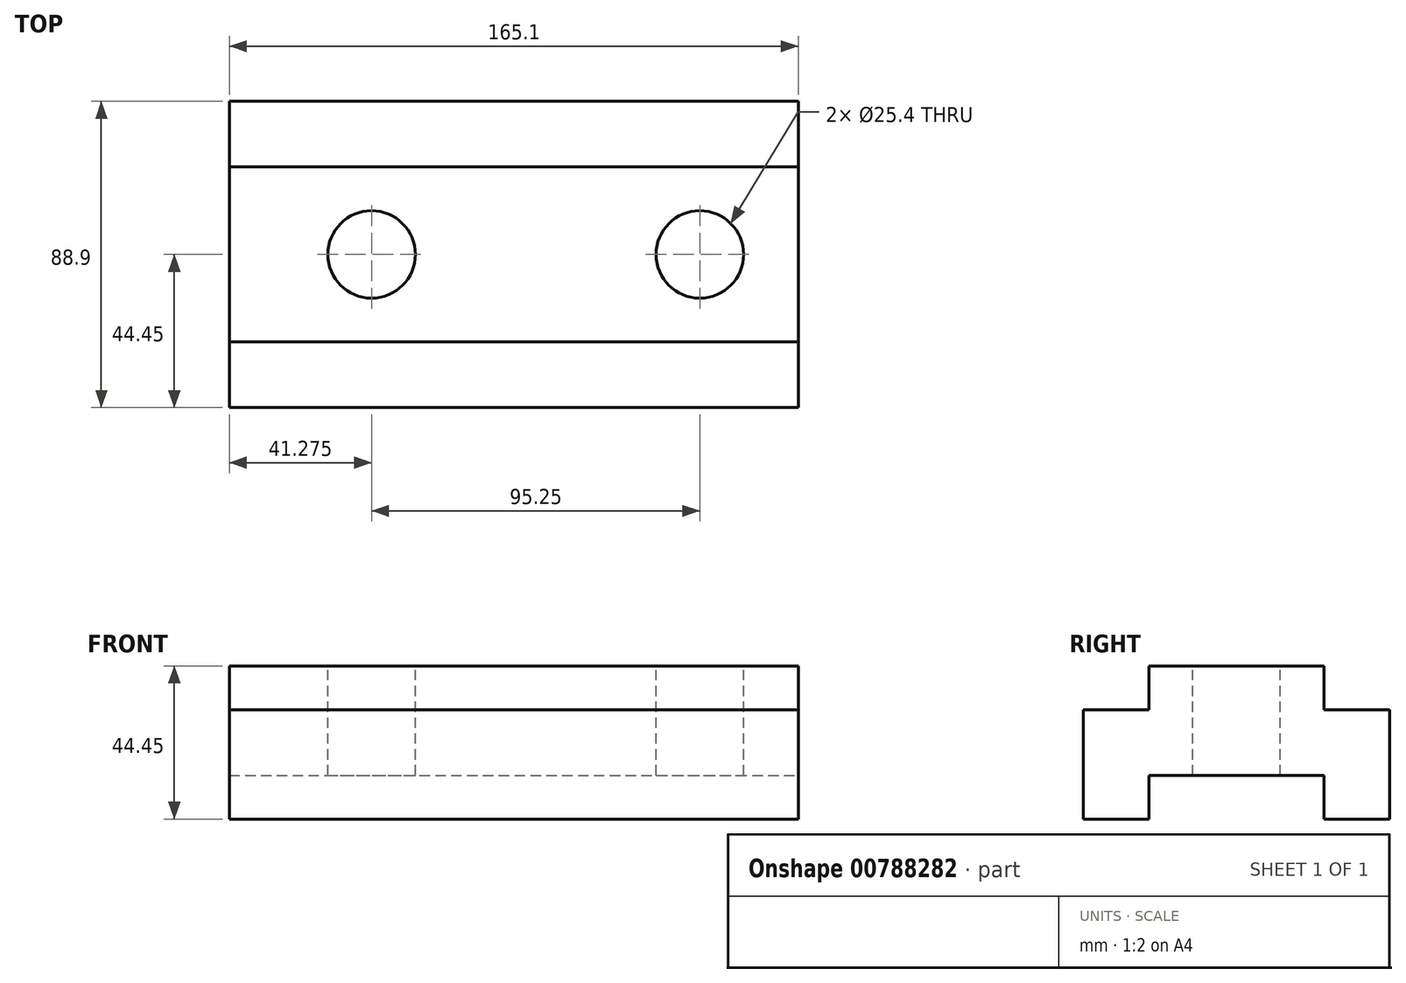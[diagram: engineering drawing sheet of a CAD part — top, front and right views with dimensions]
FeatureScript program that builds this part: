
annotation { "Feature Type Name" : "Feature", "Feature Type Description" : "" }
export const myFeature = defineFeature(function(context is Context, id is Id, definition is map)
    precondition{}
    {
        {
            var Q0;
            Q0=qCreatedBy(makeId("Right.planeOp"),FACE);
            var sketch = newSketch(context, id + "F0", { "sketchPlane" : qUnion([Q0])});
            skLineSegment(sketch, "E0", {"start": v(0, 0) * mm, "end": v(0, 31.75) * mm});
            skLineSegment(sketch, "E1", {"start": v(0, 31.75) * mm, "end": v(-19.05, 31.75) * mm});
            skLineSegment(sketch, "E2", {"start": v(-19.05, 31.75) * mm, "end": v(-19.05, 44.45) * mm});
            skLineSegment(sketch, "E3", {"start": v(-19.05, 44.45) * mm, "end": v(-69.85, 44.45) * mm});
            skLineSegment(sketch, "E4", {"start": v(-69.85, 44.45) * mm, "end": v(-69.85, 31.75) * mm});
            skLineSegment(sketch, "E5", {"start": v(-69.85, 31.75) * mm, "end": v(-88.9, 31.75) * mm});
            skLineSegment(sketch, "E6", {"start": v(-88.9, 31.75) * mm, "end": v(-88.9, 0) * mm});
            skLineSegment(sketch, "E7", {"start": v(-88.9, 0) * mm, "end": v(0, 0) * mm});
            skSolve(sketch);
        }
        {
            var Q0;
            Q0=makeQuery(id+"F0.imprint","IMPRINT",FACE,{"disambiguationData":[TD([[makeQuery(id+"F0.imprint","IMPRINT",EDGE,{"derivedFrom":sQuery(id+"F0.wireOp",EDGE,"E0")}),1.0]])]});
            extrude(context, id + "F1", {"entities" : qUnion([Q0]), "depth" : 165.1 * mm, "offsetDistance" : 25.4 * mm});
        }
        {
            var Q0;
            Q0=makeQuery(id+"F1.opExtrude","CAP_FACE",FACE,{"disambiguationData":[OSD([sQuery(id+"F0.wireOp",EDGE,"E0"),sQuery(id+"F0.wireOp",EDGE,"E1"),sQuery(id+"F0.wireOp",EDGE,"E2"),sQuery(id+"F0.wireOp",EDGE,"E3"),sQuery(id+"F0.wireOp",EDGE,"E4"),sQuery(id+"F0.wireOp",EDGE,"E5"),sQuery(id+"F0.wireOp",EDGE,"E6"),sQuery(id+"F0.wireOp",EDGE,"E7")])],"isStart":false});
            var sketch = newSketch(context, id + "F2", { "sketchPlane" : qUnion([Q0])});
            skLineSegment(sketch, "E8", {"start": v(-88.9, 0) * mm, "end": v(-69.85, 0) * mm});
            skLineSegment(sketch, "E9", {"start": v(-69.85, 0) * mm, "end": v(-69.85, 12.7) * mm});
            skLineSegment(sketch, "E10", {"start": v(-69.85, 12.7) * mm, "end": v(-19.05, 12.7) * mm});
            skLineSegment(sketch, "E11", {"start": v(-19.05, 12.7) * mm, "end": v(-19.05, 0) * mm});
            skLineSegment(sketch, "E12", {"start": v(-19.05, 0) * mm, "end": v(0, 0) * mm});
            skSolve(sketch);
        }
        {
            var Q0;
            {var subQ0=sQuery(id+"F2.wireOp",EDGE,"E9");Q0=makeQuery(id+"F2.imprint","IMPRINT",FACE,{"disambiguationData":[TD([[makeQuery(id+"F2.imprint","IMPRINT",EDGE,{"derivedFrom":subQ0}),-1.0]])]});}
            extrude(context, id + "F3", {"entities" : qUnion([Q0]), "operationType" : NewBodyOperationType.REMOVE, "oppositeDirection" : true, "depth" : 165.1 * mm, "offsetDistance" : 25.4 * mm});
        }
        {
            var Q0;
            Q0=makeQuery(id+"F1.opExtrude","SWEPT_FACE",FACE,{"disambiguationData":[OSD([sQuery(id+"F0.wireOp",EDGE,"E3")])]});
            var sketch = newSketch(context, id + "F4", { "sketchPlane" : qUnion([Q0])});
            skLineSegment(sketch, "E13", {"start": v(0, -19.05) * mm, "end": v(0, -44.45) * mm, "construction": true});
            skLineSegment(sketch, "E14", {"start": v(0, -44.45) * mm, "end": v(41.28, -44.45) * mm, "construction": true});
            skLineSegment(sketch, "E15", {"start": v(41.28, -44.45) * mm, "end": v(136.53, -44.45) * mm, "construction": true});
            skCircle(sketch, "E16", {"center": v(41.28, -44.45) * mm, "radius": 12.7 * mm});
            skCircle(sketch, "E17", {"center": v(136.53, -44.45) * mm, "radius": 12.7 * mm});
            skSolve(sketch);
        }
        {
            var Q0;
            Q0=makeQuery(id+"F4.imprint","IMPRINT",FACE,{"disambiguationData":[TD([[makeQuery(id+"F4.imprint","IMPRINT",EDGE,{"derivedFrom":sQuery(id+"F4.wireOp",EDGE,"E16")}),1.0]])]});
            var Q1;
            Q1=makeQuery(id+"F4.imprint","IMPRINT",FACE,{"disambiguationData":[TD([[makeQuery(id+"F4.imprint","IMPRINT",EDGE,{"derivedFrom":sQuery(id+"F4.wireOp",EDGE,"E17")}),1.0]])]});
            extrude(context, id + "F5", {"entities" : qUnion([Q0, Q1]), "operationType" : NewBodyOperationType.REMOVE, "endBound" : BoundingType.UP_TO_NEXT, "oppositeDirection" : true, "depth" : 25.4 * mm, "offsetDistance" : 25.4 * mm});
        }
    });
